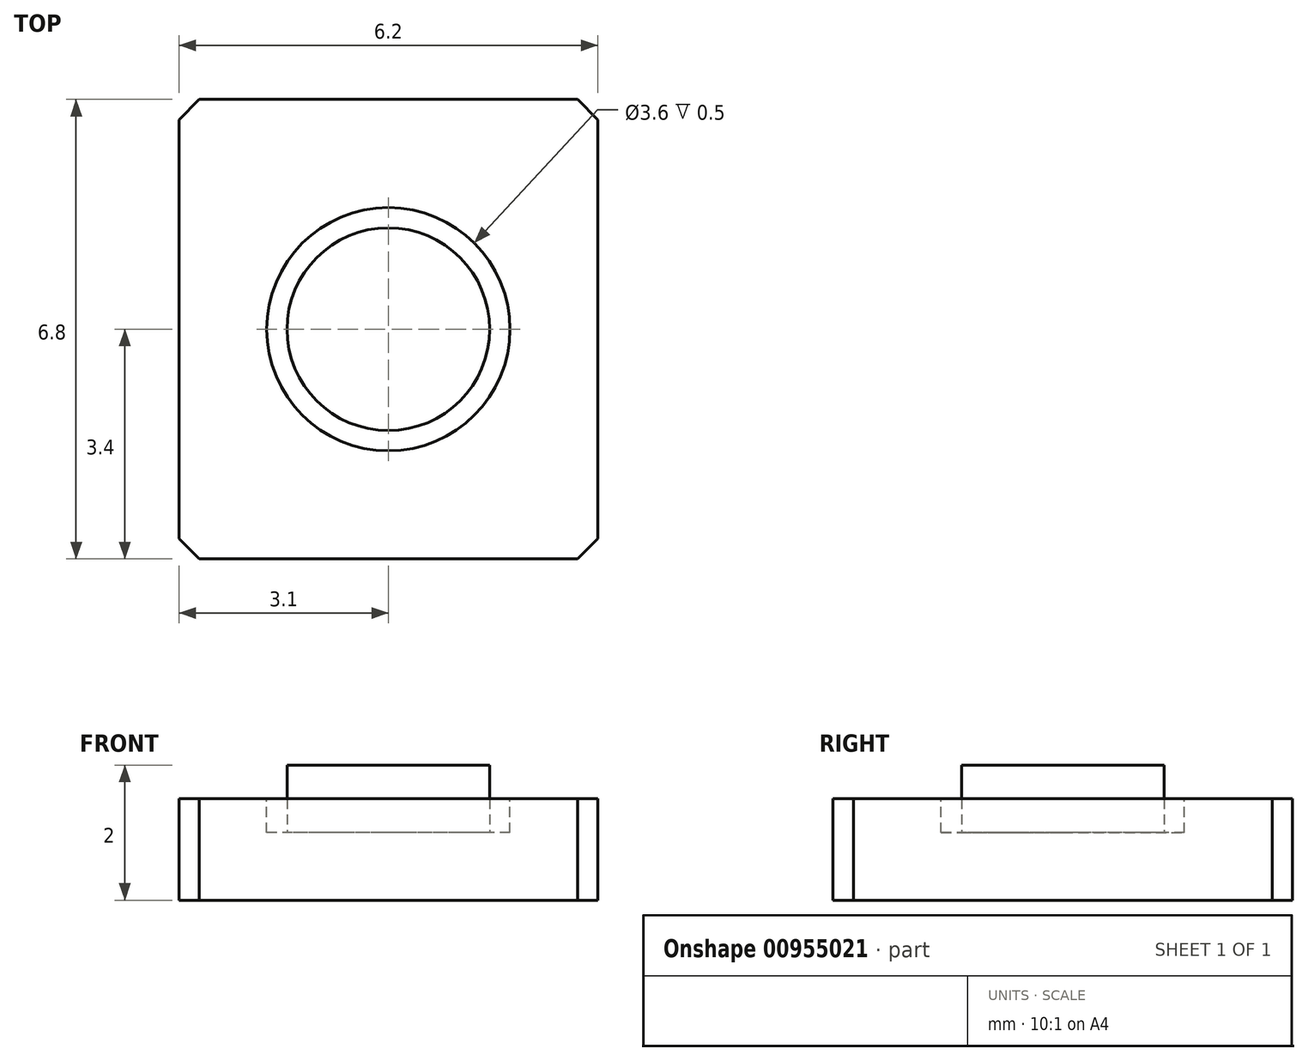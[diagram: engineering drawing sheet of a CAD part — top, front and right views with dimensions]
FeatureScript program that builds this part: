
annotation { "Feature Type Name" : "Feature", "Feature Type Description" : "" }
export const myFeature = defineFeature(function(context is Context, id is Id, definition is map)
    precondition{}
    {
        {
            var Q0;
            Q0=qCreatedBy(makeId("Top.planeOp"),FACE);
            var sketch = newSketch(context, id + "F0", { "sketchPlane" : qUnion([Q0])});
            skLineSegment(sketch, "E0.bottom", {"start": v(3.1, 3.4) * mm, "end": v(-3.1, 3.4) * mm});
            skLineSegment(sketch, "E0.top", {"start": v(3.1, -3.4) * mm, "end": v(-3.1, -3.4) * mm});
            skLineSegment(sketch, "E0.left", {"start": v(3.1, 3.4) * mm, "end": v(3.1, -3.4) * mm});
            skLineSegment(sketch, "E0.right", {"start": v(-3.1, 3.4) * mm, "end": v(-3.1, -3.4) * mm});
            skPoint(sketch, "E0.middle", {"position": v(0, 0) * mm});
            skSolve(sketch);
        }
        {
            var Q0;
            Q0 = qSketchRegion(id + "F0", true);
            extrude(context, id + "F1", {"entities" : qUnion([Q0]), "depth" : 1.5 * mm, "offsetDistance" : 25 * mm});
        }
        {
            var Q0;
            Q0=makeQuery(id+"F1.opExtrude","CAP_FACE",FACE,{"disambiguationData":[OSD([sQuery(id+"F0.wireOp",EDGE,"E0.bottom"),sQuery(id+"F0.wireOp",EDGE,"E0.top"),sQuery(id+"F0.wireOp",EDGE,"E0.left"),sQuery(id+"F0.wireOp",EDGE,"E0.right")])],"isStart":false});
            var sketch = newSketch(context, id + "F2", { "sketchPlane" : qUnion([Q0])});
            skCircle(sketch, "E1", {"center": v(0, 0) * mm, "radius": 1.8 * mm});
            skSolve(sketch);
        }
        {
            var Q0;
            Q0 = qSketchRegion(id + "F2", true);
            extrude(context, id + "F3", {"entities" : qUnion([Q0]), "operationType" : NewBodyOperationType.REMOVE, "oppositeDirection" : true, "depth" : .5 * mm, "offsetDistance" : 25 * mm});
        }
        {
            var Q0;
            Q0=makeQuery(id+"F3.boolean.opBoolean","COPY",FACE,{"derivedFrom":makeQuery(id+"F3.opExtrude","CAP_FACE",FACE,{"disambiguationData":[OSD([sQuery(id+"F2.wireOp",EDGE,"E1")])],"isStart":false})});
            var sketch = newSketch(context, id + "F4", { "sketchPlane" : qUnion([Q0])});
            skCircle(sketch, "E2", {"center": v(0, 0) * mm, "radius": 1.5 * mm});
            skSolve(sketch);
        }
        {
            var Q0;
            Q0 = qSketchRegion(id + "F4", true);
            extrude(context, id + "F5", {"entities" : qUnion([Q0]), "operationType" : NewBodyOperationType.ADD, "depth" : 1 * mm, "offsetDistance" : 25 * mm});
        }
        {
            var Q0;
            Q0=makeQuery(id+"F1.opExtrude","SWEPT_EDGE",EDGE,{"disambiguationData":[OSD([sQuery(id+"F0.wireOp",EDGE,"E0.top"),sQuery(id+"F0.wireOp",EDGE,"E0.right")])]});
            var Q1;
            Q1=makeQuery(id+"F1.opExtrude","SWEPT_EDGE",EDGE,{"disambiguationData":[OSD([sQuery(id+"F0.wireOp",EDGE,"E0.top"),sQuery(id+"F0.wireOp",EDGE,"E0.left")])]});
            var Q2;
            Q2=makeQuery(id+"F1.opExtrude","SWEPT_EDGE",EDGE,{"disambiguationData":[OSD([sQuery(id+"F0.wireOp",EDGE,"E0.bottom"),sQuery(id+"F0.wireOp",EDGE,"E0.left")])]});
            var Q3;
            Q3=makeQuery(id+"F1.opExtrude","SWEPT_EDGE",EDGE,{"disambiguationData":[OSD([sQuery(id+"F0.wireOp",EDGE,"E0.bottom"),sQuery(id+"F0.wireOp",EDGE,"E0.right")])]});
            chamfer(context, id + "F6", {"entities" : qUnion([Q0, Q1, Q2, Q3]), "width" : .3 * mm, "tangentPropagation" : true});
        }
    });
